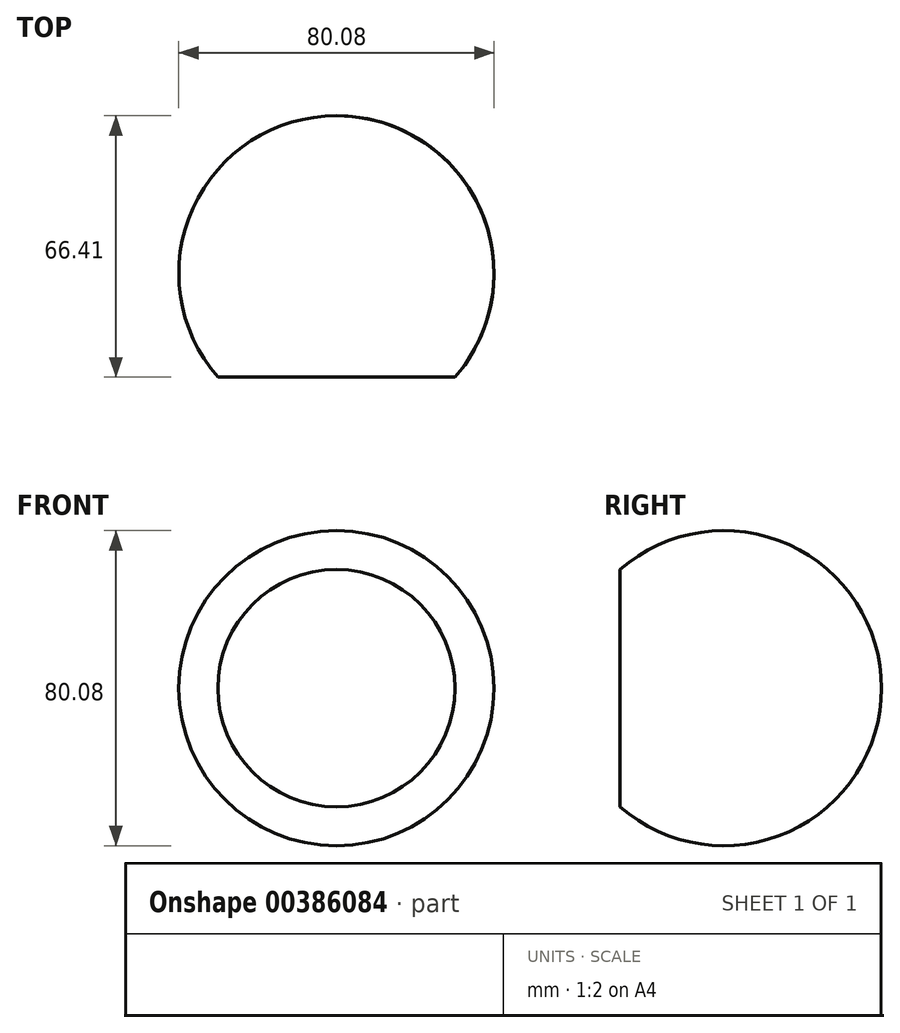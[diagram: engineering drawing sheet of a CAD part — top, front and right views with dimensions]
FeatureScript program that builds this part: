
annotation { "Feature Type Name" : "Feature", "Feature Type Description" : "" }
export const myFeature = defineFeature(function(context is Context, id is Id, definition is map)
    precondition{}
    {
        {
            var Q0;
            Q0=qCreatedBy(makeId("Top.planeOp"),FACE);
            var sketch = newSketch(context, id + "F0", { "sketchPlane" : qUnion([Q0])});
            skArc(sketch, "E0", {"start": v(30.13, -26.37) * mm, "mid": v(36.46, 16.55) * mm, "end": v(0, 40.04) * mm});
            skLineSegment(sketch, "E1", {"start": v(0, -26.37) * mm, "end": v(30.13, -26.37) * mm});
            skLineSegment(sketch, "E2", {"start": v(0, 49.83) * mm, "end": v(0, -47.1) * mm});
            skSolve(sketch);
        }
        {
            var Q0;
            Q0=sQuery(id+"F0.wireOp",EDGE,"E0");
            var Q1;
            Q1=sQuery(id+"F0.wireOp",EDGE,"E1");
            var Q2;
            Q2=sQuery(id+"F0.wireOp",EDGE,"E2");
            revolve(context, id + "F1", {"bodyType" : ToolBodyType.SURFACE, "surfaceEntities" : qUnion([Q0, Q1]), "axis" : qUnion([Q2]), "revolveType" : RevolveType.FULL});
        }
    });
